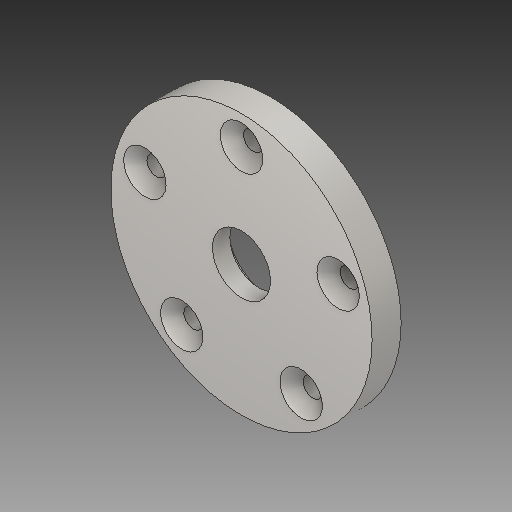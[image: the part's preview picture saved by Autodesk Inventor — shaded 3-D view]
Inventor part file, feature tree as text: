
AUTODESK INVENTOR PART (.ipt)
format: ipt  version: 2019 (Build 230136000, 136)  size: 169,984 bytes
history: native  units: mm
features: hole x2, sketch x2, extrude x1, chamfer x1, pattern_circular x1
ambient origin geometry x8: Origin, YZ Plane, XZ Plane, XY Plane, X Axis, Y Axis, Z Axis, Center Point
bodies: Solid1 (feature_tree)
feature tree (7):
  extrude  "Extrusion1"  Depth=20.0mm
  hole  "Hole1"  [1 undecoded]
  hole  "Hole2"  [1 undecoded]
  chamfer  "Chamfer1"  Distance=50.0mm Angle=360.0deg
  pattern_circular  "Circular Pattern1"  [2 undecoded]
  sketch  "Sketch1"  dims[d0=90.0mm d1=20.0mm]
  sketch  "Sketch2"  dims[d2=10.0mm d3=0.0mm d13=10.0mm d14=10.0mm d6=30.0mm d7=6.0mm d8=4.0mm d9=2.0mm d10=90.0deg d11=4.0mm d12=0.0mm d15=35.0mm d16=6.6mm d17=6.0mm d18=12.0mm d19=2.0mm d20=90.0deg d21=4.0mm d22=0.0mm d23=4.0mm d24=2.0mm d25=45.0deg d26=50.0mm d27=360.0deg]
note: 4 required parameter values undecoded (feature->parameter linkage not recoverable at this tier; creation-order binding heuristic only, values carry confidence <= 0.55)
